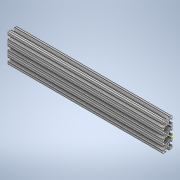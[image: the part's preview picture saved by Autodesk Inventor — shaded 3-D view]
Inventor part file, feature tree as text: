
AUTODESK INVENTOR PART (.ipt)
format: ipt  version: 2020 (Build 240168000, 168)  size: 384,000 bytes
history: native  units: in
note: dims shown in document units (in); Inventor stores cm internally (conversion verified against a paired STEP export)
features: sketch x2, extrude x1
ambient origin geometry x8: Origin, YZ Plane, XZ Plane, XY Plane, X Axis, Y Axis, Z Axis, Center Point
bodies: Solid1 (feature_tree)
feature tree (3):
  extrude  "Extrusion1"  [1 undecoded]
  sketch  "Sketch2"
  sketch  "Sketch1"  dims[d0=16.0in d1=0.0in]
note: 1 required parameter value undecoded (feature->parameter linkage not recoverable at this tier; creation-order binding heuristic only, values carry confidence <= 0.55)
